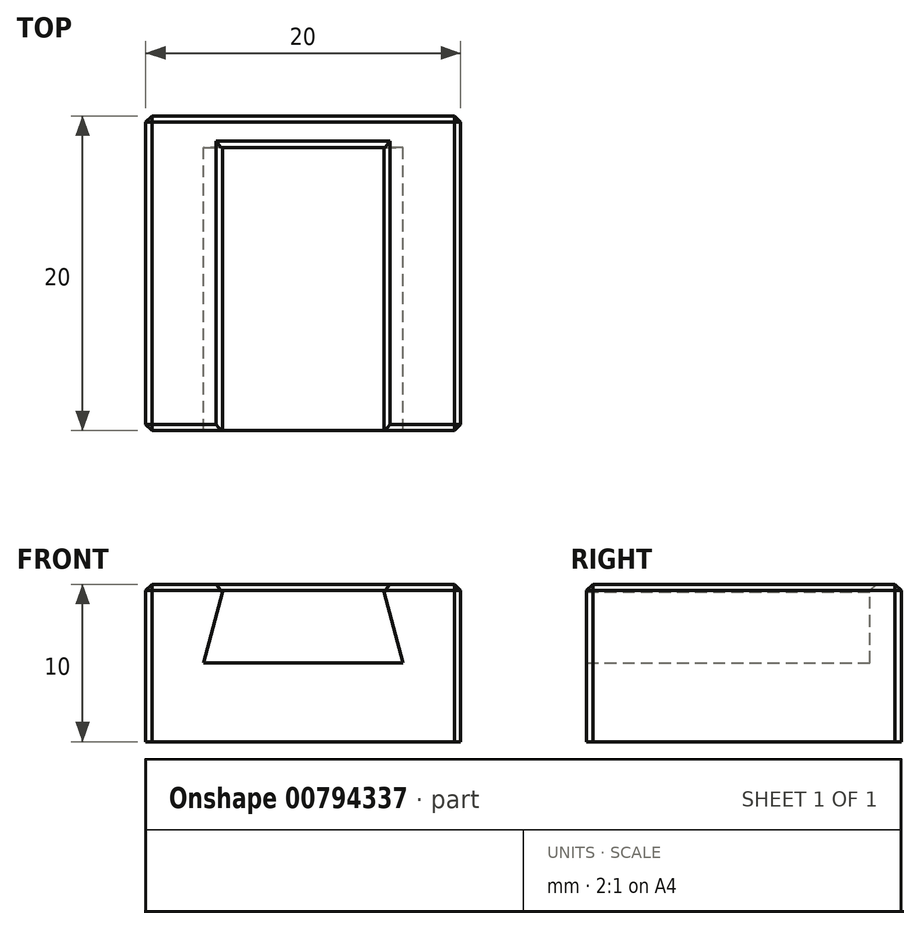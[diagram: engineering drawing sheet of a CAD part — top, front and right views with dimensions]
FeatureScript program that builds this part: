
annotation { "Feature Type Name" : "Feature", "Feature Type Description" : "" }
export const myFeature = defineFeature(function(context is Context, id is Id, definition is map)
    precondition{}
    {
        {
            assignVariable(context, id + "F0", {"name" : "PrintOffset", "anyValue" : 0.4});
        }
        {
            assignVariable(context, id + "F1", {"name" : "DovetailBackstopDepth", "anyValue" : 2});
        }
        {
            assignVariable(context, id + "F2", {"name" : "DovetailDepth", "anyValue" : 20});
        }
        {
            var Q0;
            Q0=qCreatedBy(makeId("Front.planeOp"),FACE);
            var sketch = newSketch(context, id + "F3", { "sketchPlane" : qUnion([Q0])});
            skLineSegment(sketch, "E0", {"start": v(-10, 0) * mm, "end": v(10, 0) * mm});
            skLineSegment(sketch, "E1", {"start": v(-10, 0) * mm, "end": v(-10, 10) * mm});
            skLineSegment(sketch, "E2", {"start": v(-10, 10) * mm, "end": v(-5, 10) * mm});
            skLineSegment(sketch, "E3", {"start": v(-5, 10) * mm, "end": v(-6.34, 5) * mm});
            skLineSegment(sketch, "E4", {"start": v(-6.34, 5) * mm, "end": v(6.34, 5) * mm});
            skLineSegment(sketch, "E5", {"start": v(6.34, 5) * mm, "end": v(5, 10) * mm});
            skLineSegment(sketch, "E6", {"start": v(5, 10) * mm, "end": v(10, 10) * mm});
            skLineSegment(sketch, "E7", {"start": v(10, 10) * mm, "end": v(10, 0) * mm});
            skPoint(sketch, "E8", {"position": v(0, 5) * mm});
            skLineSegment(sketch, "E9", {"start": v(-5, 10) * mm, "end": v(5, 10) * mm});
            skSolve(sketch);
        }
        {
            var Q0;
            Q0=makeQuery(id+"F3.imprint","IMPRINT",FACE,{"disambiguationData":[TD([[makeQuery(id+"F3.imprint","IMPRINT",EDGE,{"derivedFrom":sQuery(id+"F3.wireOp",EDGE,"E0")}),1.0]])]});
            extrude(context, id + "F4", {"entities" : qUnion([Q0]), "depth" : (getVariable(context, 'DovetailDepth')) * mm, "offsetDistance" : 25 * mm});
        }
        {
            var Q0;
            Q0=makeQuery(id+"F3.imprint","IMPRINT",FACE,{"disambiguationData":[TD([[makeQuery(id+"F3.imprint","IMPRINT",EDGE,{"derivedFrom":sQuery(id+"F3.wireOp",EDGE,"E3")}),1.0]])]});
            extrude(context, id + "F5", {"entities" : qUnion([Q0]), "operationType" : NewBodyOperationType.ADD, "depth" : (getVariable(context, 'DovetailBackstopDepth')) * mm, "offsetDistance" : 25 * mm});
        }
        {
            var Q0;
            Q0=makeQuery(id+"F4.opExtrude","CAP_EDGE",EDGE,{"disambiguationData":[OSD([sQuery(id+"F3.wireOp",EDGE,"E1")])],"isStart":false});
            var Q1;
            Q1=makeQuery(id+"F4.opExtrude","CAP_EDGE",EDGE,{"disambiguationData":[OSD([sQuery(id+"F3.wireOp",EDGE,"E7")])],"isStart":false});
            var Q2;
            Q2=makeQuery(id+"F4.opExtrude","CAP_EDGE",EDGE,{"disambiguationData":[OSD([sQuery(id+"F3.wireOp",EDGE,"E7")])],"isStart":true});
            var Q3;
            Q3=makeQuery(id+"F4.opExtrude","CAP_EDGE",EDGE,{"disambiguationData":[OSD([sQuery(id+"F3.wireOp",EDGE,"E1")])],"isStart":true});
            var Q4;
            Q4=makeQuery(id+"F5.boolean.opBoolean","MERGE",EDGE,{"derivedFrom":[makeQuery(id+"F4.opExtrude","CAP_EDGE",EDGE,{"disambiguationData":[OSD([sQuery(id+"F3.wireOp",EDGE,"E2")])],"isStart":true}),makeQuery(id+"F4.opExtrude","CAP_EDGE",EDGE,{"disambiguationData":[OSD([sQuery(id+"F3.wireOp",EDGE,"E6")])],"isStart":true}),makeQuery(id+"F5.opExtrude","CAP_EDGE",EDGE,{"disambiguationData":[OSD([sQuery(id+"F3.wireOp",EDGE,"E9")])],"isStart":true})]});
            var Q5;
            Q5=makeQuery(id+"F4.opExtrude","SWEPT_EDGE",EDGE,{"disambiguationData":[OSD([sQuery(id+"F3.wireOp",EDGE,"E1"),sQuery(id+"F3.wireOp",EDGE,"E2")])]});
            var Q6;
            Q6=makeQuery(id+"F4.opExtrude","SWEPT_EDGE",EDGE,{"disambiguationData":[OSD([sQuery(id+"F3.wireOp",EDGE,"E6"),sQuery(id+"F3.wireOp",EDGE,"E7")])]});
            var Q7;
            Q7=makeQuery(id+"F4.opExtrude","CAP_EDGE",EDGE,{"disambiguationData":[OSD([sQuery(id+"F3.wireOp",EDGE,"E2")])],"isStart":false});
            var Q8;
            Q8=makeQuery(id+"F4.opExtrude","CAP_EDGE",EDGE,{"disambiguationData":[OSD([sQuery(id+"F3.wireOp",EDGE,"E6")])],"isStart":false});
            var Q9;
            Q9=makeQuery(id+"F4.opExtrude","SWEPT_EDGE",EDGE,{"disambiguationData":[OSD([sQuery(id+"F3.wireOp",EDGE,"E2"),sQuery(id+"F3.wireOp",EDGE,"E3"),sQuery(id+"F3.wireOp",EDGE,"E9")])]});
            var Q10;
            Q10=makeQuery(id+"F5.opExtrude","CAP_EDGE",EDGE,{"disambiguationData":[OSD([sQuery(id+"F3.wireOp",EDGE,"E9")])],"isStart":false});
            var Q11;
            Q11=makeQuery(id+"F4.opExtrude","SWEPT_EDGE",EDGE,{"disambiguationData":[OSD([sQuery(id+"F3.wireOp",EDGE,"E5"),sQuery(id+"F3.wireOp",EDGE,"E6"),sQuery(id+"F3.wireOp",EDGE,"E9")])]});
            chamfer(context, id + "F6", {"entities" : qUnion([Q0, Q1, Q2, Q3, Q4, Q5, Q6, Q7, Q8, Q9, Q10, Q11]), "width" : (getVariable(context, 'PrintOffset')) * mm, "tangentPropagation" : true});
        }
    });
